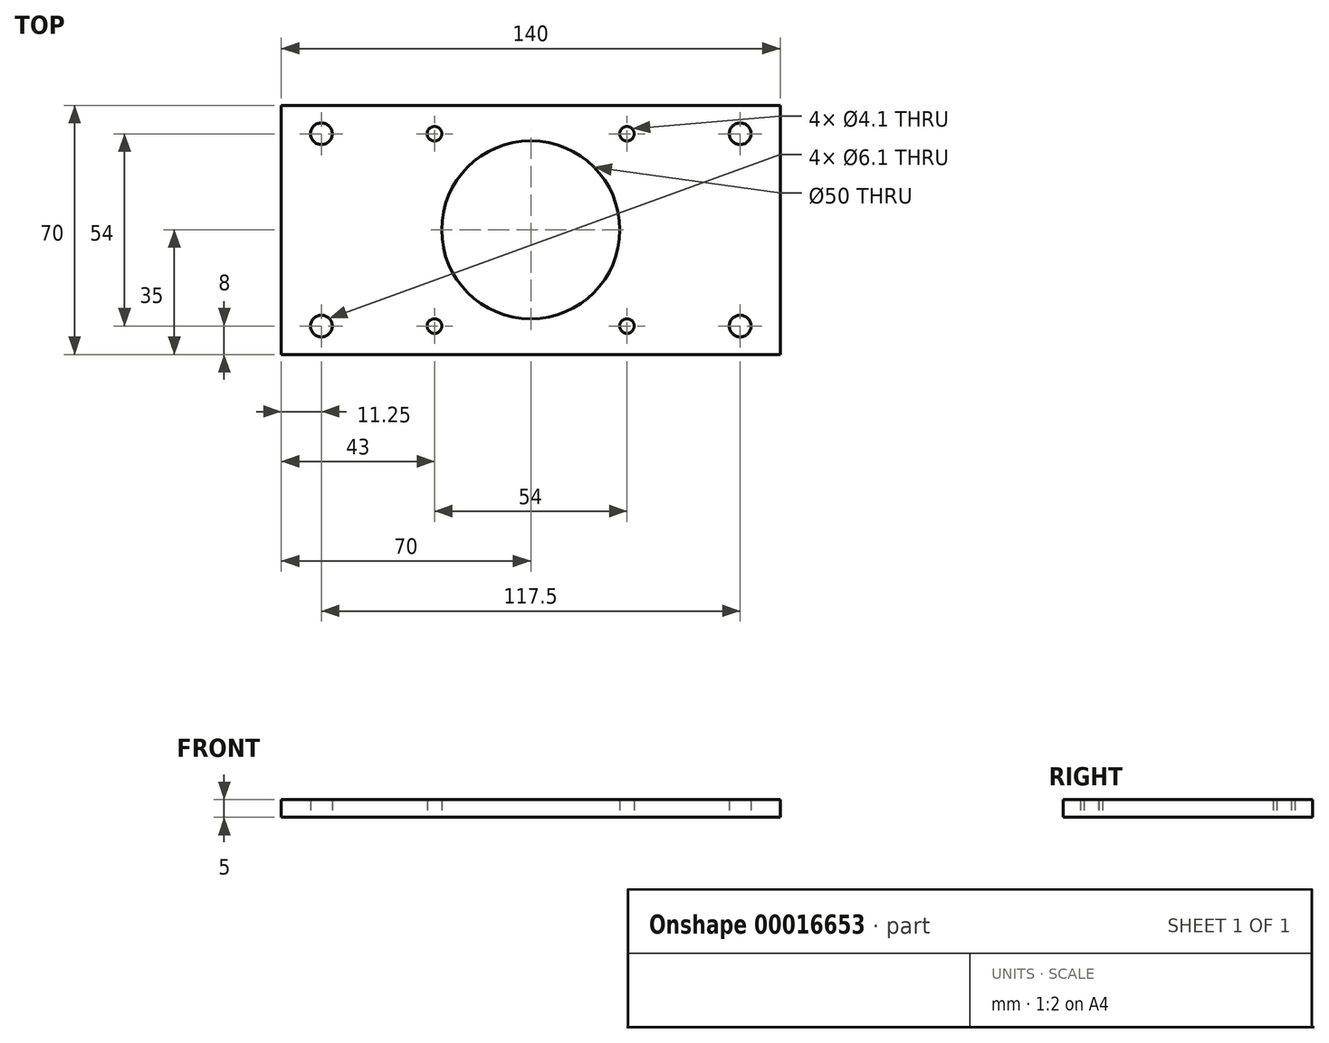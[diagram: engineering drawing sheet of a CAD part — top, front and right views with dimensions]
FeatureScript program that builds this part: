
annotation { "Feature Type Name" : "Feature", "Feature Type Description" : "" }
export const myFeature = defineFeature(function(context is Context, id is Id, definition is map)
    precondition{}
    {
        {
            var Q0;
            Q0=qCreatedBy(makeId("Top.planeOp"),FACE);
            var sketch = newSketch(context, id + "F0", { "sketchPlane" : qUnion([Q0])});
            skLineSegment(sketch, "E0.rect.bottom", {"start": v(70, -35) * mm, "end": v(-70, -35) * mm});
            skLineSegment(sketch, "E0.rect.top", {"start": v(70, 35) * mm, "end": v(-70, 35) * mm});
            skLineSegment(sketch, "E0.rect.left", {"start": v(70, -35) * mm, "end": v(70, 35) * mm});
            skLineSegment(sketch, "E0.rect.right", {"start": v(-70, -35) * mm, "end": v(-70, 35) * mm});
            skPoint(sketch, "E0.rect.middle", {"position": v(0, 0) * mm});
            skCircle(sketch, "E1", {"center": v(0, 0) * mm, "radius": 25 * mm});
            skLineSegment(sketch, "E2.rect.bottom", {"start": v(27, -27) * mm, "end": v(-27, -27) * mm, "construction": true});
            skLineSegment(sketch, "E2.rect.top", {"start": v(27, 27) * mm, "end": v(-27, 27) * mm, "construction": true});
            skLineSegment(sketch, "E2.rect.left", {"start": v(27, -27) * mm, "end": v(27, 27) * mm, "construction": true});
            skLineSegment(sketch, "E2.rect.right", {"start": v(-27, -27) * mm, "end": v(-27, 27) * mm, "construction": true});
            skCircle(sketch, "E3", {"center": v(-27, 27) * mm, "radius": 2.05 * mm});
            skCircle(sketch, "E4", {"center": v(27, 27) * mm, "radius": 2.05 * mm});
            skCircle(sketch, "E5", {"center": v(27, -27) * mm, "radius": 2.05 * mm});
            skCircle(sketch, "E6", {"center": v(-27, -27) * mm, "radius": 2.05 * mm});
            skLineSegment(sketch, "E7", {"start": v(0, 50.86) * mm, "end": v(0, -45.8) * mm, "construction": true});
            skCircle(sketch, "E8", {"center": v(-58.75, 27) * mm, "radius": 3.05 * mm});
            skCircle(sketch, "E9.MirrorC", {"center": v(58.75, 27) * mm, "radius": 3.05 * mm});
            skLineSegment(sketch, "E10", {"start": v(-73.75, 0) * mm, "end": v(74.27, 0) * mm, "construction": true});
            skCircle(sketch, "E11.MirrorC", {"center": v(58.75, -27) * mm, "radius": 3.05 * mm});
            skCircle(sketch, "E12.MirrorC", {"center": v(-58.75, -27) * mm, "radius": 3.05 * mm});
            skSolve(sketch);
        }
        {
            var Q0;
            Q0 = qSketchRegion(id + "F0", true);
            extrude(context, id + "F1", {"entities" : qUnion([Q0]), "depth" : 5 * mm});
        }
    });
